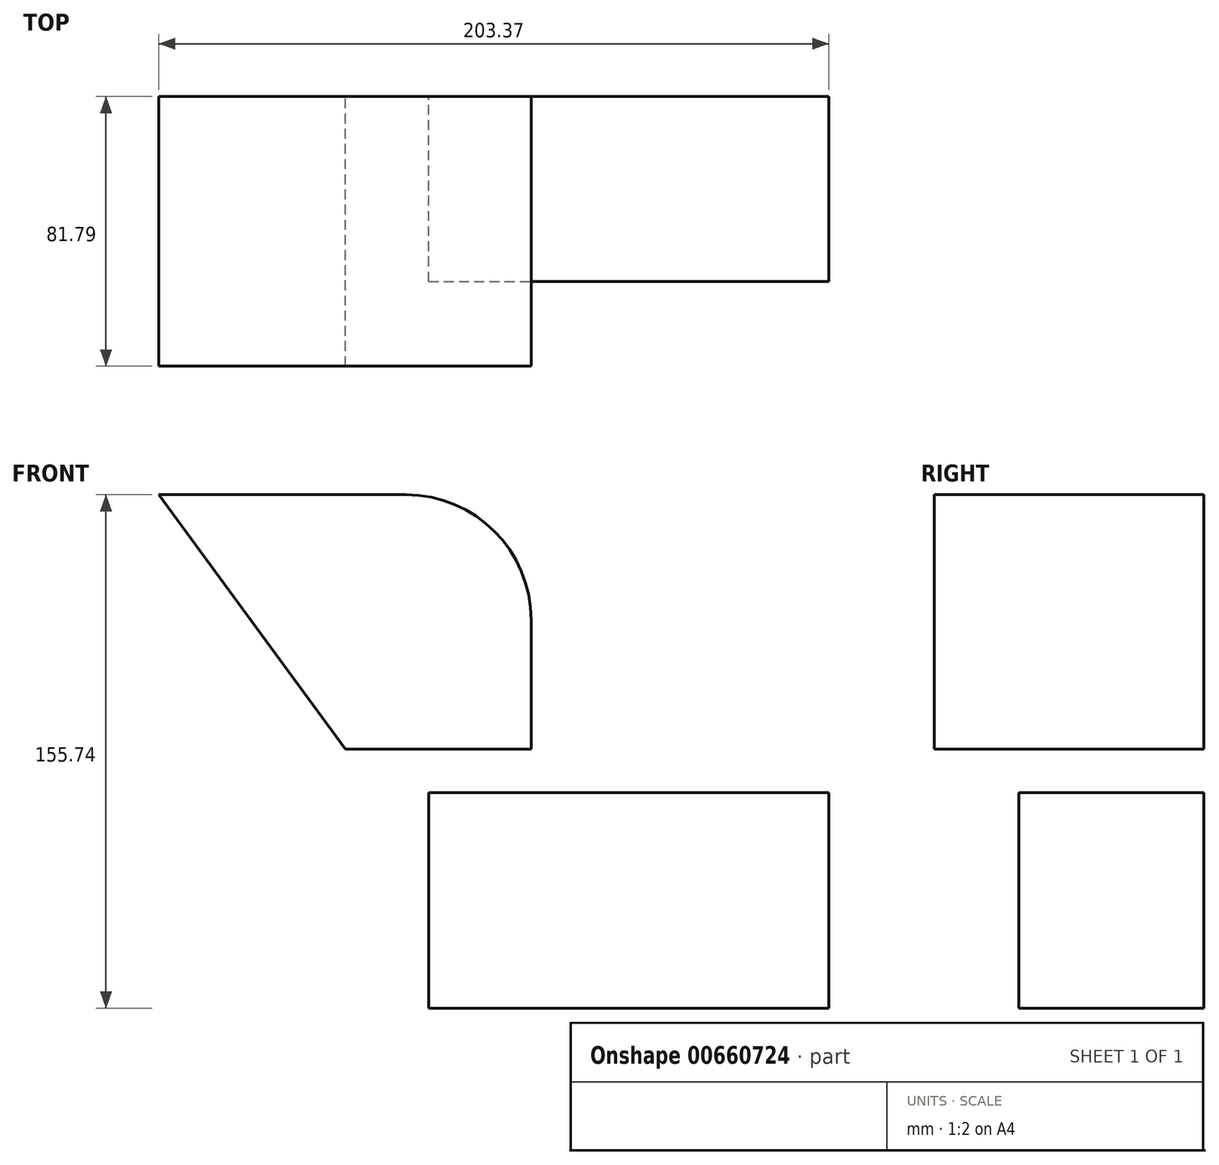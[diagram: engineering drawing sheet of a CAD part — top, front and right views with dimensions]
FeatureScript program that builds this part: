
annotation { "Feature Type Name" : "Feature", "Feature Type Description" : "" }
export const myFeature = defineFeature(function(context is Context, id is Id, definition is map)
    precondition{}
    {
        {
            var Q0;
            Q0=qCreatedBy(makeId("Front.planeOp"),FACE);
            var sketch = newSketch(context, id + "F0", { "sketchPlane" : qUnion([Q0])});
            skLineSegment(sketch, "E0", {"start": v(-56.66, 37.8) * mm, "end": v(56.38, 37.8) * mm});
            skLineSegment(sketch, "E1", {"start": v(56.38, 37.8) * mm, "end": v(56.38, -39.43) * mm});
            skLineSegment(sketch, "E2", {"start": v(56.38, -39.43) * mm, "end": v(0, -39.43) * mm});
            skLineSegment(sketch, "E3", {"start": v(0, -39.43) * mm, "end": v(-56.66, 37.8) * mm});
            skSolve(sketch);
        }
        {
            var Q0;
            Q0=makeQuery(id+"F0.imprint","IMPRINT",FACE,{"disambiguationData":[TD([[makeQuery(id+"F0.imprint","IMPRINT",EDGE,{"derivedFrom":sQuery(id+"F0.wireOp",EDGE,"E0")}),-1.0]])]});
            extrude(context, id + "F1", {"entities" : qUnion([Q0]), "depth" : 81.8 * mm, "offsetDistance" : 25.4 * mm});
        }
        {
            var Q0;
            Q0=makeQuery(id+"F1.opExtrude","SWEPT_EDGE",EDGE,{"disambiguationData":[OSD([sQuery(id+"F0.wireOp",EDGE,"E0"),sQuery(id+"F0.wireOp",EDGE,"E1")])]});
            fillet(context, id + "F2", {"entities" : qUnion([Q0]), "radius" : 38.02 * mm, "tangentPropagation" : true, "allowEdgeOverflow" : false});
        }
        {
            var Q0;
            Q0=qCreatedBy(makeId("Front.planeOp"),FACE);
            var sketch = newSketch(context, id + "F3", { "sketchPlane" : qUnion([Q0])});
            skLineSegment(sketch, "E4.bottom", {"start": v(25.3, -52.58) * mm, "end": v(146.71, -52.58) * mm});
            skLineSegment(sketch, "E4.top", {"start": v(25.3, -117.94) * mm, "end": v(146.71, -117.94) * mm});
            skLineSegment(sketch, "E4.left", {"start": v(25.3, -52.58) * mm, "end": v(25.3, -117.94) * mm});
            skLineSegment(sketch, "E4.right", {"start": v(146.71, -52.58) * mm, "end": v(146.71, -117.94) * mm});
            skSolve(sketch);
        }
        {
            var Q0;
            Q0=makeQuery(id+"F3.imprint","IMPRINT",FACE,{"disambiguationData":[TD([[makeQuery(id+"F3.imprint","IMPRINT",EDGE,{"derivedFrom":sQuery(id+"F3.wireOp",EDGE,"E4.bottom")}),-1.0]])]});
            extrude(context, id + "F4", {"entities" : qUnion([Q0]), "depth" : 56.13 * mm, "offsetDistance" : 25.4 * mm});
        }
    });
